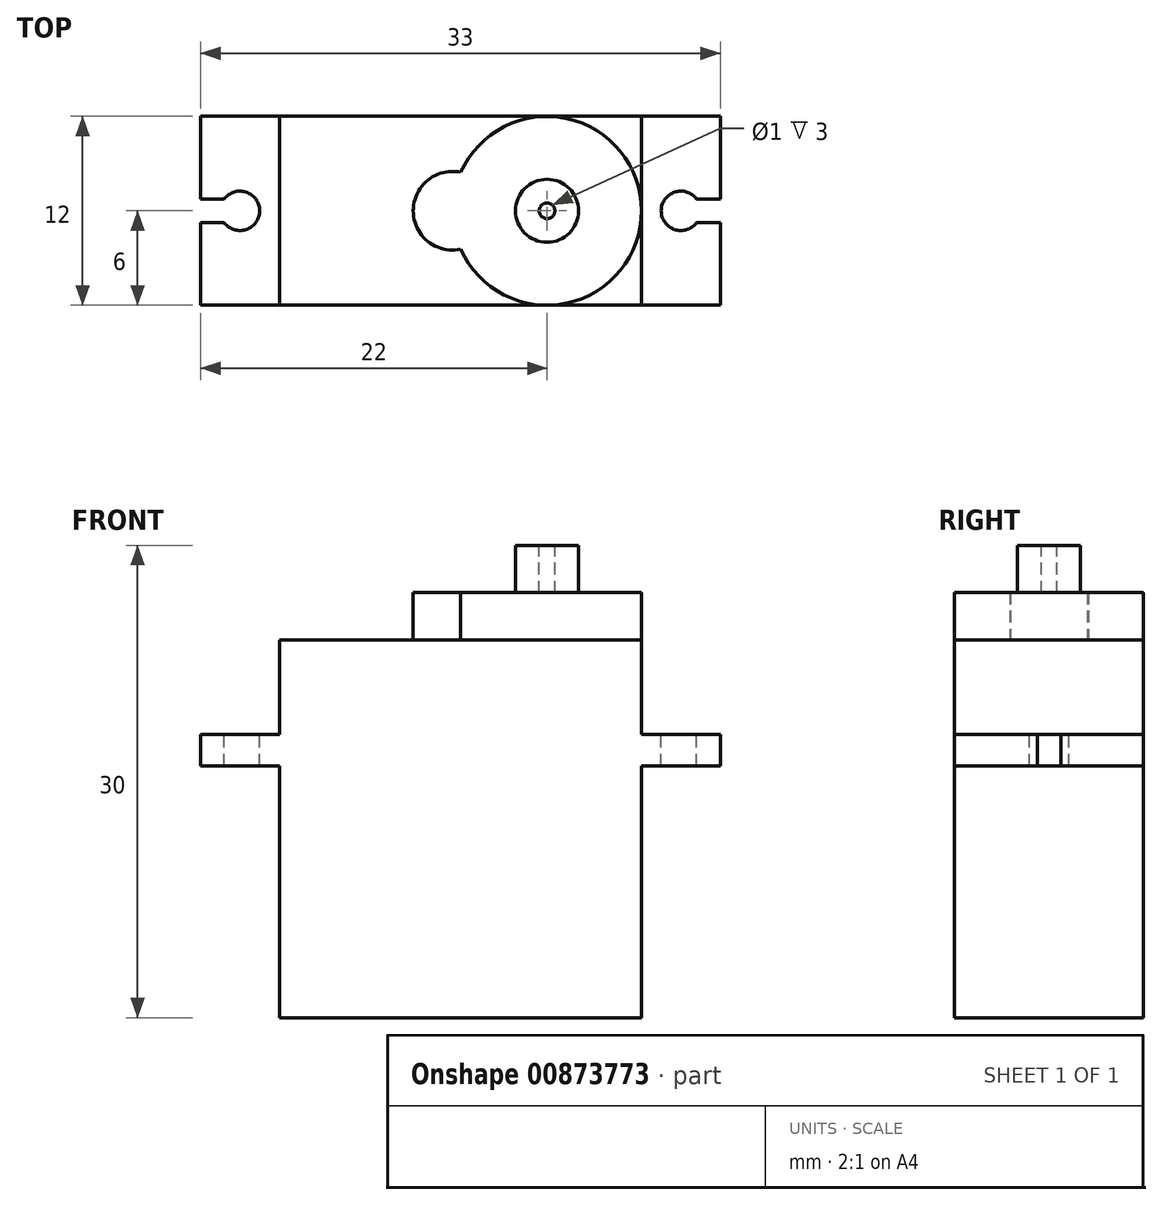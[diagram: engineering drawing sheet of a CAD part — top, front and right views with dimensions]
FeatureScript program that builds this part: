
annotation { "Feature Type Name" : "Feature", "Feature Type Description" : "" }
export const myFeature = defineFeature(function(context is Context, id is Id, definition is map)
    precondition{}
    {
        {
            var Q0;
            Q0=qCreatedBy(makeId("Top.planeOp"),FACE);
            var sketch = newSketch(context, id + "F0", { "sketchPlane" : qUnion([Q0])});
            skLineSegment(sketch, "E0.bottom", {"start": v(11.5, 6) * mm, "end": v(-11.5, 6) * mm});
            skLineSegment(sketch, "E0.top", {"start": v(11.5, -6) * mm, "end": v(-11.5, -6) * mm});
            skLineSegment(sketch, "E0.left", {"start": v(11.5, 6) * mm, "end": v(11.5, -6) * mm});
            skLineSegment(sketch, "E0.right", {"start": v(-11.5, 6) * mm, "end": v(-11.5, -6) * mm});
            skPoint(sketch, "E0.middle", {"position": v(0, 0) * mm});
            skSolve(sketch);
        }
        {
            var Q0;
            Q0 = qSketchRegion(id + "F0", true);
            extrude(context, id + "F1", {"entities" : qUnion([Q0]), "depth" : 16 * mm, "offsetDistance" : 25 * mm});
        }
        {
            var Q0;
            Q0=makeQuery(id+"F1.opExtrude","CAP_FACE",FACE,{"disambiguationData":[OSD([sQuery(id+"F0.wireOp",EDGE,"E0.bottom"),sQuery(id+"F0.wireOp",EDGE,"E0.top"),sQuery(id+"F0.wireOp",EDGE,"E0.left"),sQuery(id+"F0.wireOp",EDGE,"E0.right")])],"isStart":false});
            var sketch = newSketch(context, id + "F2", { "sketchPlane" : qUnion([Q0])});
            skLineSegment(sketch, "E1.bottom", {"start": v(-16.5, 6) * mm, "end": v(16.5, 6) * mm});
            skLineSegment(sketch, "E1.top", {"start": v(-16.5, -6) * mm, "end": v(16.5, -6) * mm});
            skLineSegment(sketch, "E1.left", {"start": v(-16.5, 6) * mm, "end": v(-16.5, -6) * mm});
            skLineSegment(sketch, "E1.right", {"start": v(16.5, 6) * mm, "end": v(16.5, -6) * mm});
            skPoint(sketch, "E1.middle", {"position": v(0, 0) * mm});
            skSolve(sketch);
        }
        {
            var Q0;
            Q0 = qSketchRegion(id + "F2", true);
            extrude(context, id + "F3", {"entities" : qUnion([Q0]), "operationType" : NewBodyOperationType.ADD, "depth" : 2 * mm, "offsetDistance" : 25 * mm});
        }
        {
            var Q0;
            Q0=makeQuery(id+"F3.opExtrude","CAP_FACE",FACE,{"disambiguationData":[OSD([sQuery(id+"F2.wireOp",EDGE,"E1.bottom"),sQuery(id+"F2.wireOp",EDGE,"E1.top"),sQuery(id+"F2.wireOp",EDGE,"E1.left"),sQuery(id+"F2.wireOp",EDGE,"E1.right")])],"isStart":false});
            var sketch = newSketch(context, id + "F4", { "sketchPlane" : qUnion([Q0])});
            skLineSegment(sketch, "E2.bottom", {"start": v(11.5, 6) * mm, "end": v(-11.5, 6) * mm});
            skLineSegment(sketch, "E2.top", {"start": v(11.5, -6) * mm, "end": v(-11.5, -6) * mm});
            skLineSegment(sketch, "E2.left", {"start": v(11.5, 6) * mm, "end": v(11.5, -6) * mm});
            skLineSegment(sketch, "E2.right", {"start": v(-11.5, 6) * mm, "end": v(-11.5, -6) * mm});
            skPoint(sketch, "E2.middle", {"position": v(0, 0) * mm});
            skSolve(sketch);
        }
        {
            var Q0;
            Q0 = qSketchRegion(id + "F4", true);
            extrude(context, id + "F5", {"entities" : qUnion([Q0]), "operationType" : NewBodyOperationType.ADD, "depth" : 6 * mm, "offsetDistance" : 25 * mm});
        }
        {
            var Q0;
            Q0=makeQuery(id+"F5.opExtrude","CAP_FACE",FACE,{"disambiguationData":[OSD([sQuery(id+"F4.wireOp",EDGE,"E2.bottom"),sQuery(id+"F4.wireOp",EDGE,"E2.top"),sQuery(id+"F4.wireOp",EDGE,"E2.left"),sQuery(id+"F4.wireOp",EDGE,"E2.right")])],"isStart":false});
            var sketch = newSketch(context, id + "F6", { "sketchPlane" : qUnion([Q0])});
            skCircle(sketch, "E3", {"center": v(5.5, 0) * mm, "radius": 6 * mm});
            skCircle(sketch, "E4", {"center": v(-0.5, 0) * mm, "radius": 2.5 * mm});
            skSolve(sketch);
        }
        {
            var Q0;
            Q0 = qSketchRegion(id + "F6", true);
            extrude(context, id + "F7", {"entities" : qUnion([Q0]), "operationType" : NewBodyOperationType.ADD, "depth" : 3 * mm, "offsetDistance" : 25 * mm});
        }
        {
            var Q0;
            Q0=makeQuery(id+"F7.opExtrude","CAP_FACE",FACE,{"disambiguationData":[OSD([sQuery(id+"F6.wireOp",EDGE,"E3"),sQuery(id+"F6.wireOp",EDGE,"E4")])],"isStart":false});
            var sketch = newSketch(context, id + "F8", { "sketchPlane" : qUnion([Q0])});
            skCircle(sketch, "E5", {"center": v(5.5, 0) * mm, "radius": 2 * mm});
            skSolve(sketch);
        }
        {
            var Q0;
            Q0 = qSketchRegion(id + "F8", true);
            extrude(context, id + "F9", {"entities" : qUnion([Q0]), "operationType" : NewBodyOperationType.ADD, "depth" : 3 * mm, "offsetDistance" : 25 * mm});
        }
        {
            var Q0;
            {var subQ0=sQuery(id+"F2.wireOp",EDGE,"E1.top");var subQ1=sQuery(id+"F2.wireOp",EDGE,"E1.bottom");var subQ2=sQuery(id+"F2.wireOp",EDGE,"E1.left");Q0=makeQuery(id+"F5.boolean.opBoolean","SPLIT",FACE,{"disambiguationData":[TD([makeQuery(id+"F3.opExtrude","SWEPT_FACE",FACE,{"disambiguationData":[OSD([subQ2])]})])],"derivedFrom":makeQuery(id+"F3.opExtrude","CAP_FACE",FACE,{"disambiguationData":[OSD([subQ1,subQ0,subQ2,sQuery(id+"F2.wireOp",EDGE,"E1.right")])],"isStart":false})});}
            var sketch = newSketch(context, id + "F10", { "sketchPlane" : qUnion([Q0])});
            skCircle(sketch, "E6", {"center": v(-14, 0) * mm, "radius": 1.25 * mm});
            skCircle(sketch, "E7", {"center": v(14, 0) * mm, "radius": 1.25 * mm});
            skLineSegment(sketch, "E8.bottom", {"start": v(-16.5, -0.75) * mm, "end": v(-15, -0.75) * mm});
            skLineSegment(sketch, "E8.top", {"start": v(-16.5, 0.75) * mm, "end": v(-15, 0.75) * mm});
            skLineSegment(sketch, "E8.left", {"start": v(-16.5, -0.75) * mm, "end": v(-16.5, 0.75) * mm});
            skLineSegment(sketch, "E8.right", {"start": v(-15, -0.75) * mm, "end": v(-15, 0.75) * mm});
            skLineSegment(sketch, "E9.bottom", {"start": v(15, 0.75) * mm, "end": v(16.5, 0.75) * mm});
            skLineSegment(sketch, "E9.top", {"start": v(15, -0.75) * mm, "end": v(16.5, -0.75) * mm});
            skLineSegment(sketch, "E9.left", {"start": v(15, 0.75) * mm, "end": v(15, -0.75) * mm});
            skLineSegment(sketch, "E9.right", {"start": v(16.5, 0.75) * mm, "end": v(16.5, -0.75) * mm});
            skSolve(sketch);
        }
        {
            var Q0;
            Q0 = qSketchRegion(id + "F10", true);
            extrude(context, id + "F11", {"entities" : qUnion([Q0]), "operationType" : NewBodyOperationType.REMOVE, "endBound" : BoundingType.THROUGH_ALL, "oppositeDirection" : true, "depth" : 25 * mm, "offsetDistance" : 25 * mm});
        }
        {
            var Q0;
            Q0=makeQuery(id+"F9.opExtrude","CAP_FACE",FACE,{"disambiguationData":[OSD([sQuery(id+"F8.wireOp",EDGE,"E5")])],"isStart":false});
            var sketch = newSketch(context, id + "F12", { "sketchPlane" : qUnion([Q0])});
            skCircle(sketch, "E10", {"center": v(5.5, 0) * mm, "radius": 0.5 * mm});
            skSolve(sketch);
        }
        {
            var Q0;
            Q0 = qSketchRegion(id + "F12", true);
            extrude(context, id + "F13", {"entities" : qUnion([Q0]), "operationType" : NewBodyOperationType.REMOVE, "oppositeDirection" : true, "depth" : 3 * mm, "offsetDistance" : 25 * mm});
        }
    });
